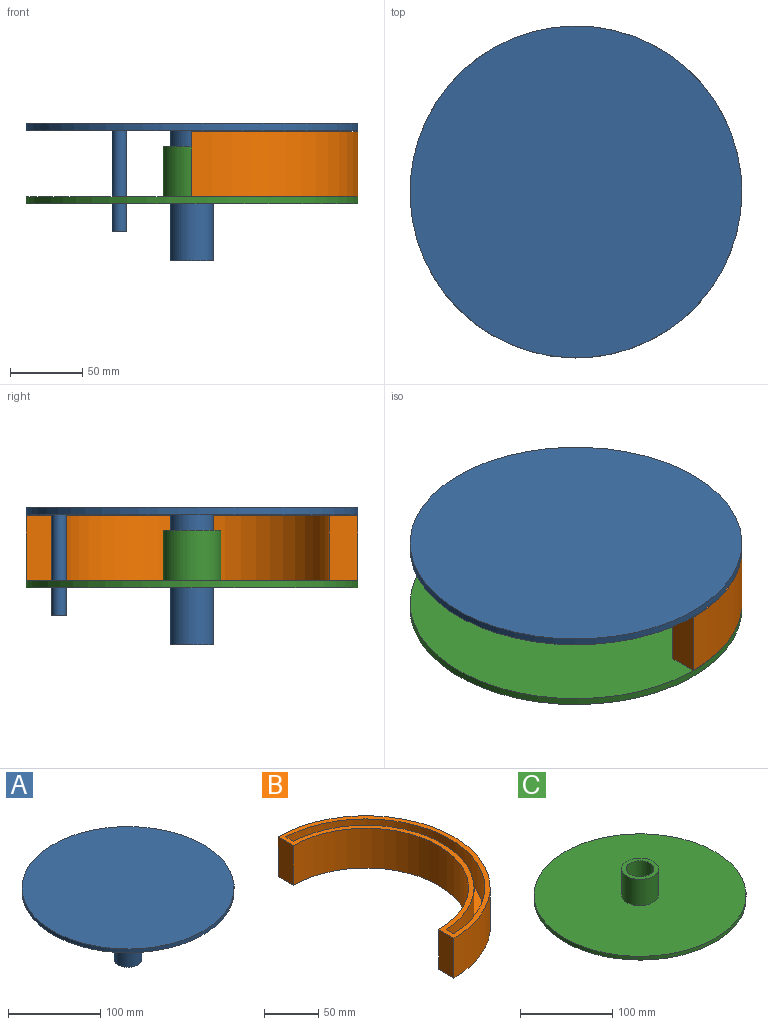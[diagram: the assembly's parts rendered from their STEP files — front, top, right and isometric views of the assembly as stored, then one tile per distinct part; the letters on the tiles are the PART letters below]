
ASSEMBLY  parts=3 mates=3
PART A: 7 faces, bbox 230x230x95 mm
  f0: cylinder r=15mm len=90mm, axis (0,0,-1), area 8482.3mm2, adj f1,f4
  f1: plane 30x30mm, normal (0,0,-1), area 706.9mm2, adj f0
  f2: cylinder r=115mm len=230mm, axis (0,0,-1), area 3612.8mm2, adj f3,f4
  f3: plane 230x230mm, normal (0,0,1), area 41547.6mm2, adj f2
  f4: plane 230x230mm, normal (0,0,-1), area 40762.2mm2, adj f0,f2,f5
  f5: cylinder r=5mm len=70mm, axis (0,0,1), area 2199.1mm2, adj f4,f6
  f6: plane 10x10mm, normal (0,0,-1), area 78.5mm2, adj f5
PART B: 11 faces, bbox 115x230x45 mm
  f0: plane 45x20mm, normal (-1,0,0), area 900mm2, adj f1,f3,f4,f9
  f1: cylinder r=115mm len=230mm, axis (0,0,-1), area 16257.7mm2, adj f0,f2,f4,f9
  f2: plane 45x20mm, normal (-1,0,0), area 900mm2, adj f1,f3,f4,f9
  f3: cylinder r=95mm len=190mm, axis (0,0,-1), area 13430.3mm2, adj f0,f2,f4,f9
  f4: plane 230x115mm, normal (0,0,-1), area 6597.3mm2, adj f0,f1,f2,f3
  f5: plane 12.47x10.01mm, normal (1,0,0), area 118.3mm2, adj f6,f8,f9,f10
  f6: cylinder r=100mm len=199.75mm, axis (0,0,-1), area 7711.5mm2, adj f5,f7,f9,f10
  f7: plane 39.53x10.01mm, normal (1,0,0), area 389.3mm2, adj f6,f8,f9,f10
  f8: cylinder r=110mm len=219.77mm, axis (0,0,-1), area 8508mm2, adj f5,f7,f9,f10
  f9: plane 230x115mm, normal (0,0,1), area 3398.7mm2, adj f0,f1,f2,f3,f5,f6,f7,f8
  f10: plane 219.77x105mm, normal (0,-0.13,0.99), area 3225.2mm2, adj f5,f6,f7,f8
PART C: 7 faces, bbox 230x230x40 mm
  f0: cylinder r=115mm len=230mm, axis (0,0,-1), area 3612.8mm2, adj f1,f2
  f1: plane 230x230mm, normal (0,0,1), area 40290.9mm2, adj f0,f4
  f2: plane 230x230mm, normal (0,0,-1), area 41547.6mm2, adj f0
  f3: cylinder r=15mm len=35mm, axis (0,0,-1), area 3298.7mm2, adj f5,f6
  f4: cylinder r=20mm len=40mm, axis (0,0,-1), area 4398.2mm2, adj f1,f5
  f5: plane 40x40mm, normal (0,0,1), area 549.8mm2, adj f3,f4
  f6: plane 30x30mm, normal (0,0,1), area 706.9mm2, adj f3
PLACE A rot(axis=(0,0,1),76.5deg) t=(95.68,40.82,-72.62)mm
PLACE B t=(95.68,40.82,-28.38)mm
PLACE C t=(95.68,40.82,-33.38)mm fixed
MATE parallel B.f1 <-> C.f0  axis (0,0,-1) through (95.68,40.82,-5.88)mm
MATE cylindrical A.f0 <-> C.f0  axis (0,0,-1) through (95.68,40.82,-72.62)mm
MATE planar C.f0 <-> B.f4  axis (0,0,1) through (95.68,40.82,-28.38)mm
